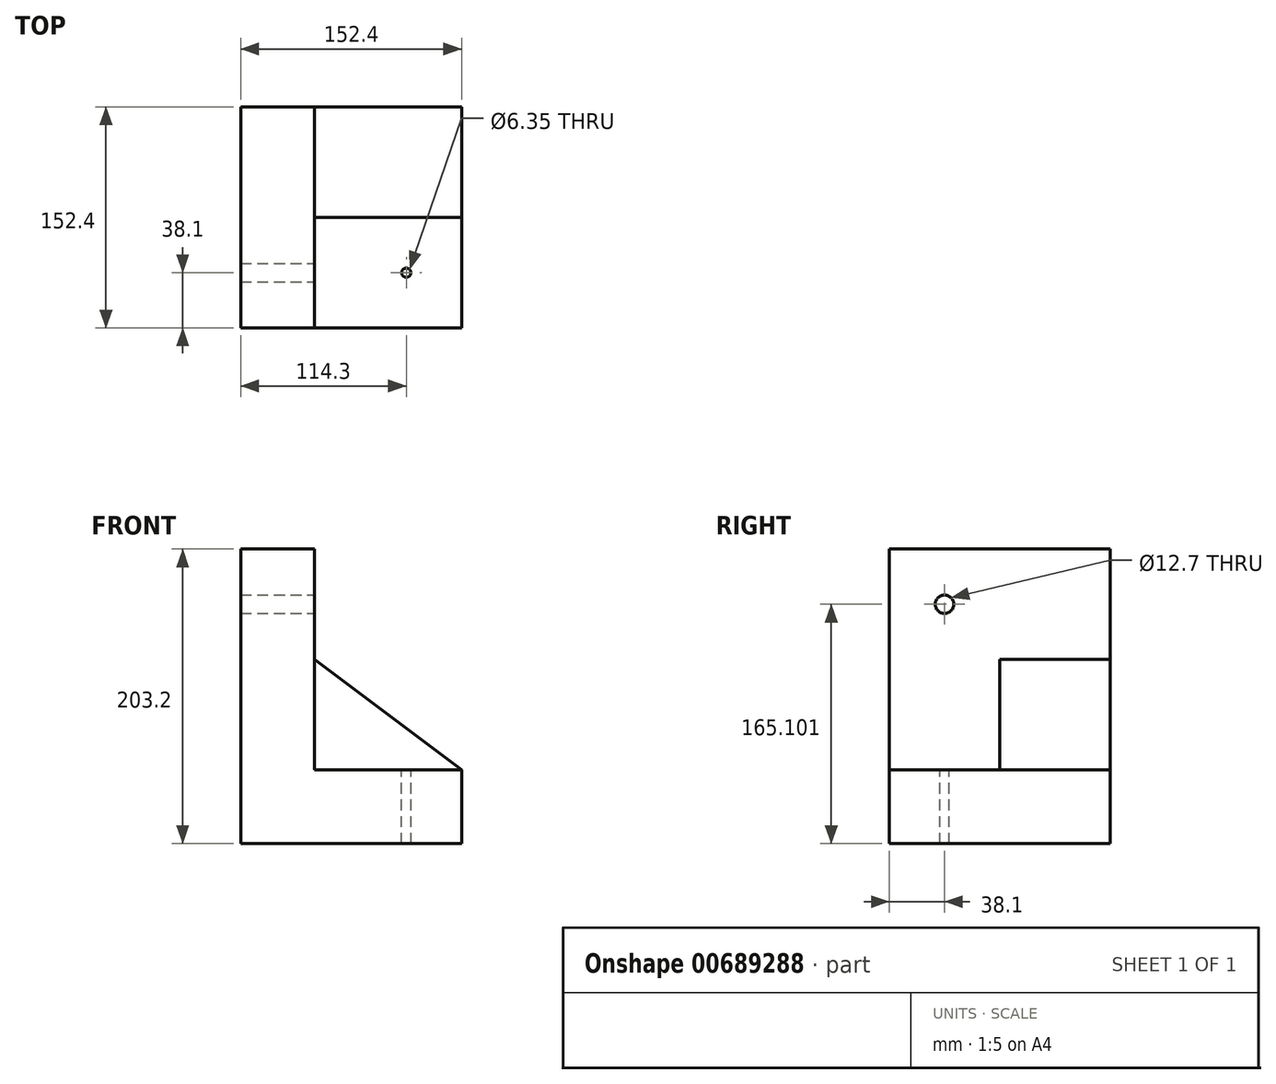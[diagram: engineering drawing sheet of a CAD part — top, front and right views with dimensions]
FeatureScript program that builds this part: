
annotation { "Feature Type Name" : "Feature", "Feature Type Description" : "" }
export const myFeature = defineFeature(function(context is Context, id is Id, definition is map)
    precondition{}
    {
        {
            var Q0;
            Q0=qCreatedBy(makeId("Front.planeOp"),FACE);
            var sketch = newSketch(context, id + "F0", { "sketchPlane" : qUnion([Q0])});
            skLineSegment(sketch, "E0", {"start": v(-50.8, 98.28) * mm, "end": v(-50.8, -104.92) * mm});
            skLineSegment(sketch, "E1", {"start": v(101.6, -104.92) * mm, "end": v(-50.8, -104.92) * mm});
            skLineSegment(sketch, "E2", {"start": v(101.6, -104.92) * mm, "end": v(101.6, -54.12) * mm});
            skLineSegment(sketch, "E3", {"start": v(-50.8, 98.28) * mm, "end": v(0, 98.28) * mm});
            skLineSegment(sketch, "E4", {"start": v(0, -54.12) * mm, "end": v(0, 98.28) * mm});
            skLineSegment(sketch, "E5", {"start": v(0, -54.12) * mm, "end": v(101.6, -54.12) * mm});
            skSolve(sketch);
        }
        {
            var Q0;
            Q0=makeQuery(id+"F0.imprint","IMPRINT",FACE,{"disambiguationData":[TD([[makeQuery(id+"F0.imprint","IMPRINT",EDGE,{"derivedFrom":sQuery(id+"F0.wireOp",EDGE,"E0")}),1.0]])]});
            var Q1;
            Q1 = qSketchRegion(id + "F0", true);
            extrude(context, id + "F1", {"entities" : qUnion([Q0, Q1]), "depth" : 152.4 * mm, "offsetDistance" : 25.4 * mm});
        }
        {
            var Q0;
            Q0=makeQuery(id+"F1.opExtrude","SWEPT_FACE",FACE,{"disambiguationData":[OSD([sQuery(id+"F0.wireOp",EDGE,"E5")])]});
            var sketch = newSketch(context, id + "F2", { "sketchPlane" : qUnion([Q0])});
            skLineSegment(sketch, "E6.bottom", {"start": v(0, 0) * mm, "end": v(101.6, 0) * mm});
            skLineSegment(sketch, "E6.top", {"start": v(0, -76.2) * mm, "end": v(101.6, -76.2) * mm});
            skLineSegment(sketch, "E6.left", {"start": v(0, 0) * mm, "end": v(0, -76.2) * mm});
            skLineSegment(sketch, "E6.right", {"start": v(101.6, 0) * mm, "end": v(101.6, -76.2) * mm});
            skSolve(sketch);
        }
        {
            var Q0;
            Q0=makeQuery(id+"F2.imprint","IMPRINT",FACE,{"disambiguationData":[TD([[makeQuery(id+"F2.imprint","IMPRINT",EDGE,{"derivedFrom":sQuery(id+"F2.wireOp",EDGE,"E6.bottom")}),-1.0]])]});
            extrude(context, id + "F3", {"entities" : qUnion([Q0]), "operationType" : NewBodyOperationType.ADD, "depth" : 76.2 * mm, "offsetDistance" : 25.4 * mm});
        }
        {
            var Q0;
            Q0=makeQuery(id+"F3.opExtrude","SWEPT_FACE",FACE,{"disambiguationData":[OSD([sQuery(id+"F2.wireOp",EDGE,"E6.top")])]});
            var sketch = newSketch(context, id + "F4", { "sketchPlane" : qUnion([Q0])});
            skLineSegment(sketch, "E7", {"start": v(0, 22.08) * mm, "end": v(101.6, -54.12) * mm});
            skLineSegment(sketch, "E8", {"start": v(101.6, -54.12) * mm, "end": v(101.6, 22.08) * mm});
            skLineSegment(sketch, "E9", {"start": v(101.6, 22.08) * mm, "end": v(0, 22.08) * mm});
            skSolve(sketch);
        }
        {
            var Q0;
            Q0=makeQuery(id+"F4.imprint","IMPRINT",FACE,{"disambiguationData":[TD([[makeQuery(id+"F4.imprint","IMPRINT",EDGE,{"derivedFrom":sQuery(id+"F4.wireOp",EDGE,"E7")}),1.0]])]});
            extrude(context, id + "F5", {"entities" : qUnion([Q0]), "operationType" : NewBodyOperationType.REMOVE, "oppositeDirection" : true, "depth" : 76.2 * mm, "offsetDistance" : 25.4 * mm});
        }
        {
            var Q0;
            Q0=makeQuery(id+"F1.opExtrude","SWEPT_FACE",FACE,{"disambiguationData":[OSD([sQuery(id+"F0.wireOp",EDGE,"E5")])]});
            var sketch = newSketch(context, id + "F6", { "sketchPlane" : qUnion([Q0])});
            skCircle(sketch, "E10", {"center": v(63.5, -114.3) * mm, "radius": 4.76 * mm});
            skSolve(sketch);
        }
        {
            var Q0;
            Q0=makeQuery(id+"F1.opExtrude","SWEPT_FACE",FACE,{"disambiguationData":[OSD([sQuery(id+"F0.wireOp",EDGE,"E4")])]});
            var sketch = newSketch(context, id + "F7", { "sketchPlane" : qUnion([Q0])});
            skPoint(sketch, "E11", {"position": v(-114.3, 60.18) * mm});
            skSolve(sketch);
        }
        {
            var Q0;
            Q0=sQuery(id+"F7.wireOp",VERTEX,"E11");
            var Q1;
            Q1=makeQuery(id+"F1.opExtrude","SWEPT_BODY",BODY,{"disambiguationData":[OSD([sQuery(id+"F0.wireOp",EDGE,"E0"),sQuery(id+"F0.wireOp",EDGE,"E1"),sQuery(id+"F0.wireOp",EDGE,"E2"),sQuery(id+"F0.wireOp",EDGE,"E3"),sQuery(id+"F0.wireOp",EDGE,"E4"),sQuery(id+"F0.wireOp",EDGE,"E5")])]});
            hole(context, id + "F8", {"style" : HoleStyle.SIMPLE, "endStyle" : HoleEndStyle.THROUGH, "holeDiameter" : 12.7 * mm, "majorDiameter" : 6.35 * mm, "isTappedThrough" : true, "tappedDepth" : 12.7 * mm, "tapClearance" : 3, "locations" : qUnion([Q0]), "scope" : qUnion([Q1])});
        }
        {
            var Q0;
            Q0=sQuery(id+"F6.wireOp",VERTEX,"E10.center");
            var Q1;
            Q1=makeQuery(id+"F1.opExtrude","SWEPT_BODY",BODY,{"disambiguationData":[OSD([sQuery(id+"F0.wireOp",EDGE,"E0"),sQuery(id+"F0.wireOp",EDGE,"E1"),sQuery(id+"F0.wireOp",EDGE,"E2"),sQuery(id+"F0.wireOp",EDGE,"E3"),sQuery(id+"F0.wireOp",EDGE,"E4"),sQuery(id+"F0.wireOp",EDGE,"E5")])]});
            hole(context, id + "F9", {"style" : HoleStyle.SIMPLE, "endStyle" : HoleEndStyle.THROUGH, "holeDiameter" : 6.35 * mm, "majorDiameter" : 6.35 * mm, "isTappedThrough" : true, "tappedDepth" : 12.7 * mm, "tapClearance" : 3, "locations" : qUnion([Q0]), "scope" : qUnion([Q1])});
        }
    });
